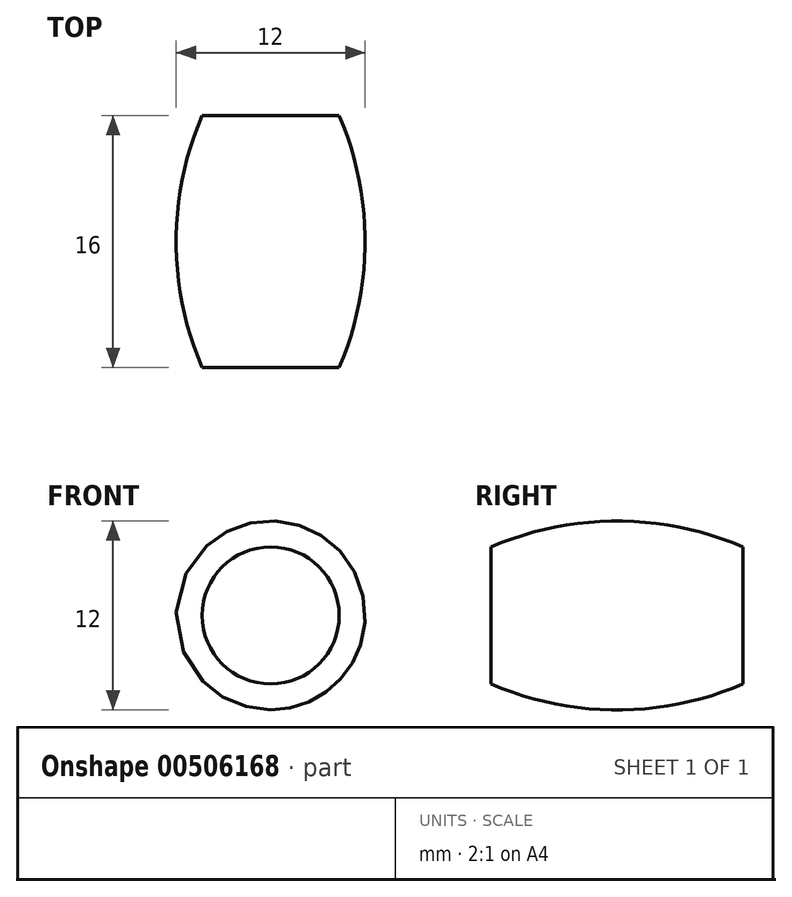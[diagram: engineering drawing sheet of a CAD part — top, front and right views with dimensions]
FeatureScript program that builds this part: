
annotation { "Feature Type Name" : "Feature", "Feature Type Description" : "" }
export const myFeature = defineFeature(function(context is Context, id is Id, definition is map)
    precondition{}
    {
        {
            var Q0;
            Q0=qCreatedBy(makeId("Right.planeOp"),FACE);
            var sketch = newSketch(context, id + "F0", { "sketchPlane" : qUnion([Q0])});
            skArc(sketch, "E0", {"start": v(8, 18.6) * mm, "mid": v(0, 20.25) * mm, "end": v(-8, 18.6) * mm});
            skLineSegment(sketch, "E1", {"start": v(-8, 14.25) * mm, "end": v(-8, 18.6) * mm});
            skLineSegment(sketch, "E2", {"start": v(8, 18.6) * mm, "end": v(8, 14.25) * mm});
            skLineSegment(sketch, "E3", {"start": v(-8, 14.25) * mm, "end": v(8, 14.25) * mm});
            skPoint(sketch, "E4", {"position": v(0, 20.25) * mm});
            skPoint(sketch, "E5.orphan", {"position": v(-8, 0) * mm});
            skPoint(sketch, "E6.orphan", {"position": v(8, 0) * mm});
            skSolve(sketch);
        }
        {
            var Q0;
            Q0=makeQuery(id+"F0.imprint","IMPRINT",FACE,{"disambiguationData":[TD([[makeQuery(id+"F0.imprint","IMPRINT",EDGE,{"derivedFrom":sQuery(id+"F0.wireOp",EDGE,"E0")}),1.0]])]});
            var Q1;
            Q1=sQuery(id+"F0.wireOp",EDGE,"E3");
            revolve(context, id + "F1", {"entities" : qUnion([Q0]), "axis" : qUnion([Q1]), "revolveType" : RevolveType.FULL});
        }
    });
